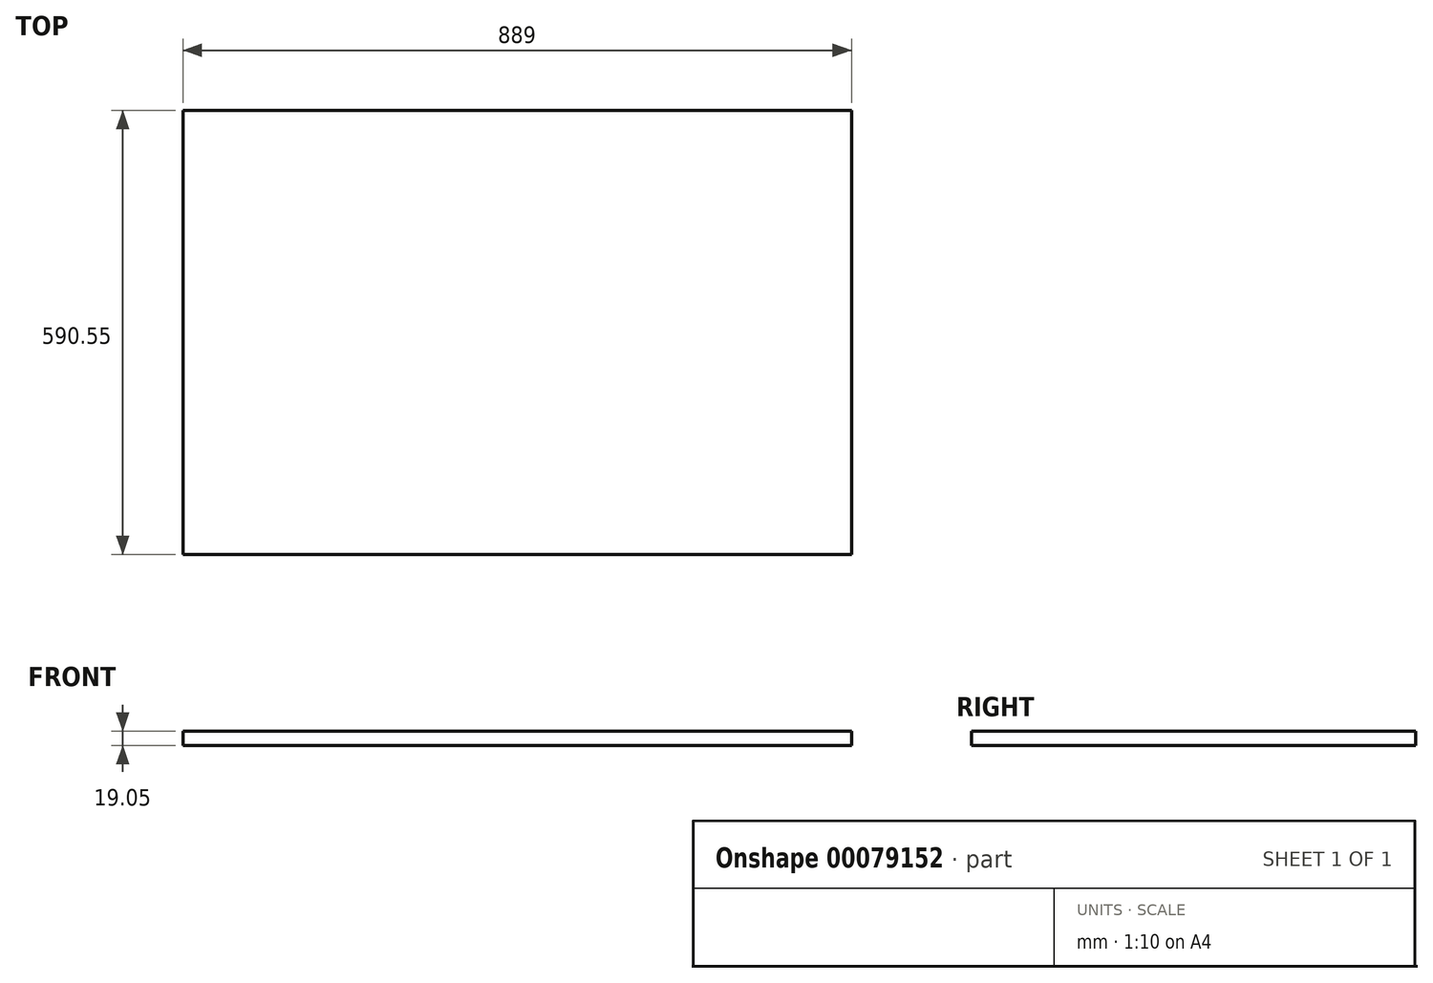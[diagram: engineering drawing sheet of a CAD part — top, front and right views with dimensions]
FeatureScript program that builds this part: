
annotation { "Feature Type Name" : "Feature", "Feature Type Description" : "" }
export const myFeature = defineFeature(function(context is Context, id is Id, definition is map)
    precondition{}
    {
        {
            var Q0;
            Q0=qCreatedBy(makeId("Top.planeOp"),FACE);
            var sketch = newSketch(context, id + "F0", { "sketchPlane" : qUnion([Q0])});
            skLineSegment(sketch, "E0.bottom", {"start": v(-825.69, 505.92) * mm, "end": v(63.31, 505.92) * mm});
            skLineSegment(sketch, "E0.top", {"start": v(-825.69, -84.63) * mm, "end": v(63.31, -84.63) * mm});
            skLineSegment(sketch, "E0.left", {"start": v(-825.69, 505.92) * mm, "end": v(-825.69, -84.63) * mm});
            skLineSegment(sketch, "E0.right", {"start": v(63.31, 505.92) * mm, "end": v(63.31, -84.63) * mm});
            skSolve(sketch);
        }
        {
            var Q0;
            Q0=makeQuery(id+"F0.imprint","IMPRINT",FACE,{"disambiguationData":[TD([[makeQuery(id+"F0.imprint","IMPRINT",EDGE,{"derivedFrom":sQuery(id+"F0.wireOp",EDGE,"E0.bottom")}),-1.0]])]});
            extrude(context, id + "F1", {"entities" : qUnion([Q0]), "depth" : 19.05 * mm});
        }
    });
